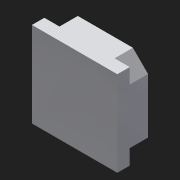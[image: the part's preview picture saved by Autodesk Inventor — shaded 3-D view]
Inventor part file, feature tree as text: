
AUTODESK INVENTOR PART (.ipt)
format: ipt  version: 2017 SP1 (Build 210196100, 196)  size: 142,336 bytes
history: native  units: in
note: dims shown in document units (in); Inventor stores cm internally (conversion verified against a paired STEP export)
features: extrude x3, sketch x3
ambient origin geometry x8: Origin, YZ Plane, XZ Plane, XY Plane, X Axis, Y Axis, Z Axis, Center Point
bodies: Solid1 (feature_tree)
feature tree (6):
  extrude  "Extrusion1"  Depth=24.4094in
  extrude  "Extrusion2"  Depth=8.7795in TaperAngle=0.0deg
  extrude  "Extrusion3"  Depth=13.3465in
  sketch  "Sketch1"  dims[d0=24.4094in d1=24.4094in]
  sketch  "Sketch2"  dims[d2=7.3031in d3=8.7795in d4=0.0in]
  sketch  "Sketch3"  dims[d5=4.3307in d6=4.3307in d7=1.5748in d9=360.0deg d11=5.2362in d12=0.0in d32=6.2992in d33=3.937in d34=3.937in d35=6.2992in d36=6.2992in d37=6.2992in d38=75.0deg d39=75.0deg d40=6.2992in d41=3.937in d42=3.937in d43=0.4134in d44=0.4134in d45=4.4488in d46=8.3858in d47=0.7874in d48=12.4016in d49=0.4134in d50=0.597in d51=7.3031in d52=13.3465in d53=0.0in]
